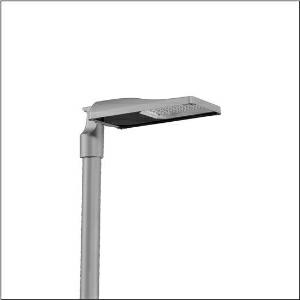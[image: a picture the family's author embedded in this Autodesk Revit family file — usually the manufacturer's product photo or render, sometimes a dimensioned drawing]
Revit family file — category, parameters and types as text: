
# Revit family: streetlight_sl_31_mini___st1_0a_5xh2d31a08ha_13ce
name_source: partatom
category: Lighting Fixtures
units: mm (PartAtom-declared; Revit-internal decimal feet)

## family parameters
Cut with Voids When Loaded = No
Host = Face
Light Source = No
Part Type = Normal
Room Calculation Point = No
Round Connector Dimension = Use Diameter
Shared = No

## types (1)
- --- (1 x LED, 9240 lm, 68.3 W, 3000K)
    Apparent Load = 68 VA
    CIE Flux Codes = 37 72 97 100 100
    Color Rendering = 70
    Color Temperature = 3000K
    Default Elevation = 1800 mm
    Description = Streetlight SL 31 mini Easy, Desk-Remote mast luminaire for post-top, side-entry; light control with lens of PMMA; light distribution: ST1.0a, direct asymmetric distribution, for standard-compliant lighting for roads and squares; LED: luminous flux: 9.240lm, light colour: 730, colour temperature: 3000K; luminous efficacy: 135,3lm/W; control: pre-setting: linear dimming characteristic, flexible luminous flux parameterisation, time-dependent luminous flux control, constant luminous flux control, intelligent temperature release in ECG and LED module, overheat protection; luminaire housing, of diecast aluminium, Siteco® metallic grey (DB 702S), corrosivity category C5 high according to DIN EN ISO 12944; cover of toughened safety glass, transparent, mast flange of diecast aluminium, Siteco® metallic grey (DB 702S), spigot size: 76/60mm, mast flange included unmounted; with cable H07RN-F 2x 1.5mm², cable length: 8,5m, connection cable pre-assembled; mains connection: 220..240V, AC, 50/60Hz; power consumption (at start of service life): 68,3W / (at end of service life): 74,8W / (with reduced operation 50%): 29,7W; protection rating (complete): IP66; insulation class (complete): insulation class II (safety insulation); impact resistance: IK10; certification: CE, ENEC, ENEC+, VDE, UKCA; permissible operating ambient temperature for outdoor applications: -40..+50°C; packaging unit: 1 piece

Light Distribution: ST1.0a
    Height = 76 mm
    Lamp = 1 x LED
    Lamp Light Flux = 9240 lm
    Lamp Power = 68.3 W
    Lamp count = 1
    Length = 547 mm
    Luminous efficacy = 135 lm/W
    Manufacturer = Siteco
    ModVariant = No
    Model = 5XH2D31A08HA
    Number of Poles = 1
    OnlyDefault = Yes
    Power Factor = 1
    Product Name = Streetlight SL 31 mini | ST1.0a
    Product group = mast luminaire | pylon top
    ProductGroupID = 6100
    Protection Class = Protection class II
    Protection Degree = IP 66
    RLX_Detail_Level = 1
    RLX_Emergency_Light_Flux = 0 lm
    RLX_Emergency_Type = 0
    RLX_Emergency_Type_DB = No
    RlxData = <blob elided: 39405 chars, md5=427684cf>
    Socket = socket
    Standby Power = 0 W
    System Light Flux = 9240 lm
    System Power = 68 W
    Type Comments = factory setting: luminous flux: 100 % | dim-lin: 254 | 693 mA
    Type Image = l_1300326.jpg
    URL = http://relux.com
    VarID = @adj_055216
    Voltage = 0 V
    Weight = 0.00 kg
    Width = 265 mm

## geometry (parser evidence)
native form markers: Blend x4, Sweep x11
no freeform markers — native parametric forms only
